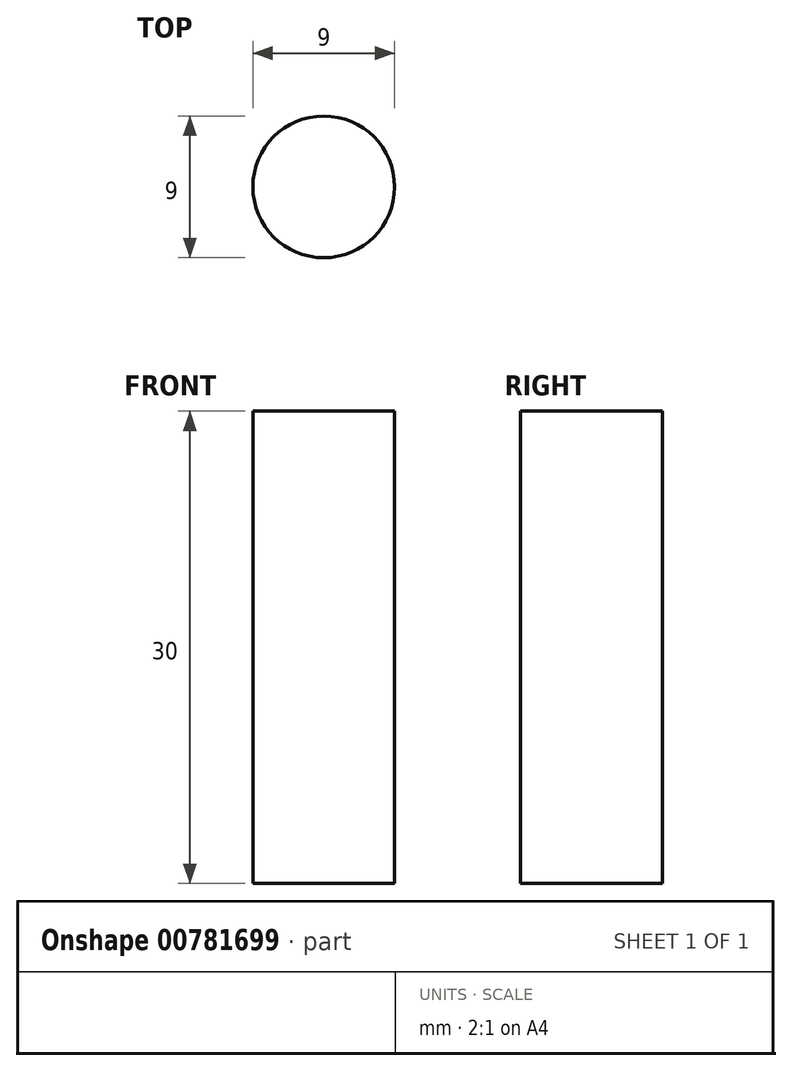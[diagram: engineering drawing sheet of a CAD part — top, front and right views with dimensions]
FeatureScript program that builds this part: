
annotation { "Feature Type Name" : "Feature", "Feature Type Description" : "" }
export const myFeature = defineFeature(function(context is Context, id is Id, definition is map)
    precondition{}
    {
        {
            var Q0;
            Q0=qCreatedBy(makeId("Top.planeOp"),FACE);
            var sketch = newSketch(context, id + "F0", { "sketchPlane" : qUnion([Q0])});
            skCircle(sketch, "E0", {"center": v(0, 0) * mm, "radius": 4.5 * mm});
            skSolve(sketch);
        }
        {
            var Q0;
            Q0=makeQuery(id+"F0.imprint","IMPRINT",FACE,{"disambiguationData":[TD([[makeQuery(id+"F0.imprint","IMPRINT",EDGE,{"derivedFrom":sQuery(id+"F0.wireOp",EDGE,"E0")}),1.0]])]});
            extrude(context, id + "F1", {"entities" : qUnion([Q0]), "depth" : 30 * mm, "offsetDistance" : 25.4 * mm});
        }
    });
